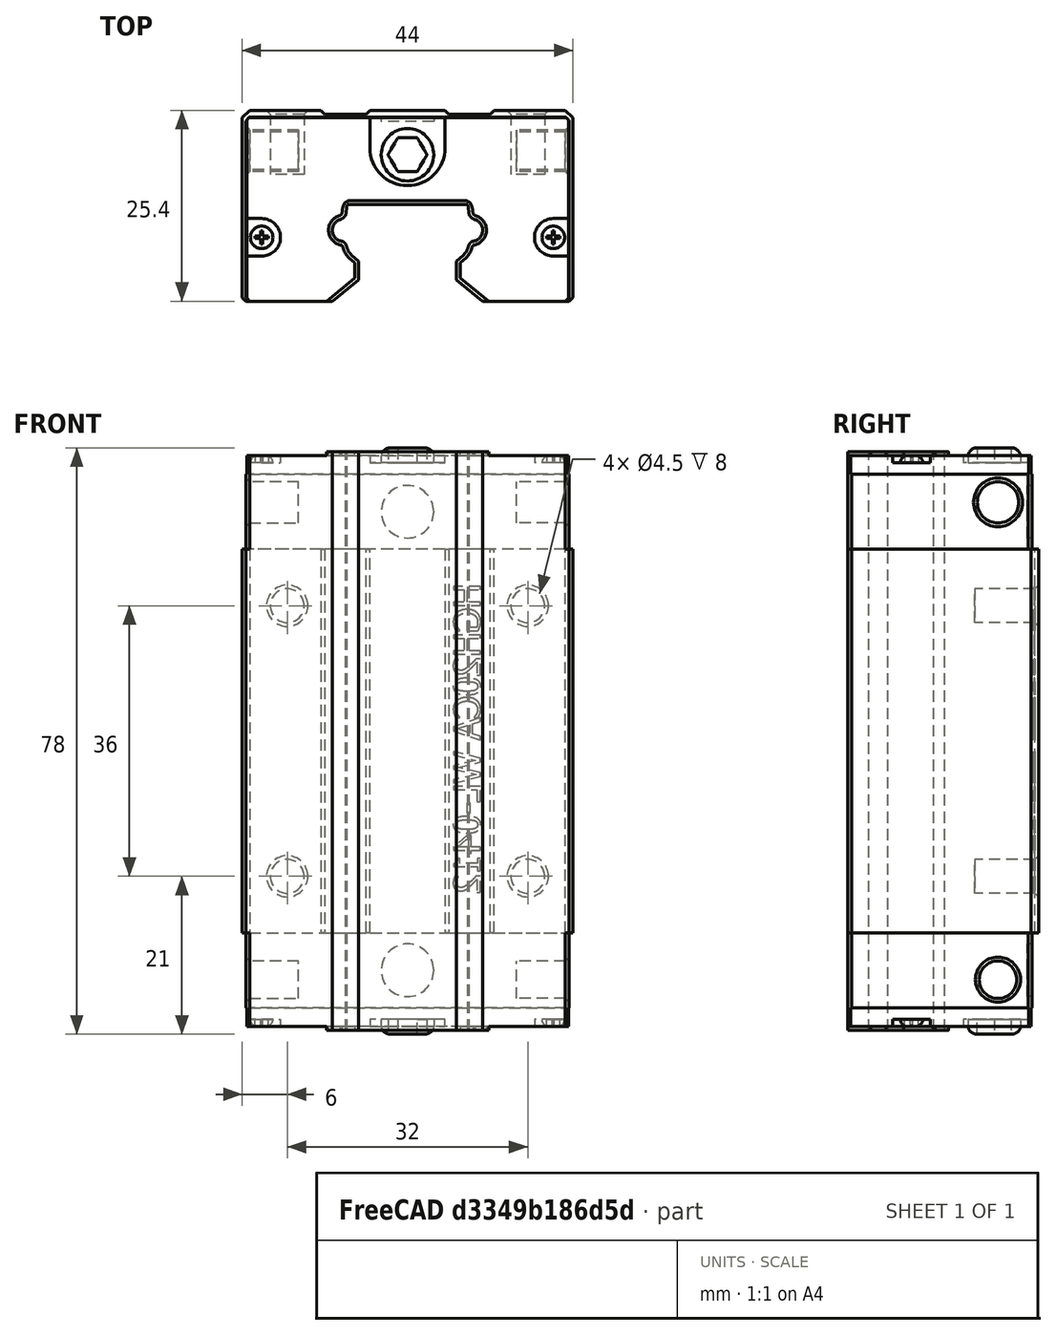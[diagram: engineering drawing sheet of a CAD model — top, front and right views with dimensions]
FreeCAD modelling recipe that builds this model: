
FCSTD DOCUMENT  (FreeCAD 0.22R37100 (Git))
Label: HGH20CA
License: All rights reserved
LicenseURL: http://en.wikipedia.org/wiki/All_rights_reserved
objects: PartDesign::CoordinateSystem×3, Part::Feature×1, PartDesign::FeatureBase×1, PartDesign::Body×1, Sketcher::SketchObject×1
note: 7 computed .brp shape members not serialized (recipe doc carries the construction recipe); baked Part::Feature solids carry a one-line shape summary decoded from their .brp

FEATURE [Part::Feature] Part__Feature004  label="HGH20CA"
  shape: bbox 44.01 x 25.41 x 78.01 mm, 462 faces (baked)
FEATURE [PartDesign::FeatureBase] BaseFeature
  BaseFeature = -> Part__Feature004
  Suppressed = false
FEATURE [PartDesign::CoordinateSystem] Local_CS
  AttacherType = Attacher::AttachEngine3D
  AttachmentSupport = -> [XY_Plane]
  MapMode = 5
FEATURE [PartDesign::CoordinateSystem] Local_CS001
  AttacherType = Attacher::AttachEngine3D
  AttachmentOffset = pos=(0,25.4,0) rot=(1,0,0;-1.5708rad)
  AttachmentSupport = -> [XY_Plane]
  MapMode = 5
  Placement = pos=(0,25.4,0) rot=(1,0,0;4.71239rad)
FEATURE [PartDesign::CoordinateSystem] Local_CS002
  AttacherType = Attacher::AttachEngine3D
  AttachmentSupport = -> [BaseFeature]
  MapMode = 5
  Placement = pos=(0,12.9,0) rot=(1,0,0;1.5708rad)
FEATURE [PartDesign::Body] Body
  BaseFeature = -> Part__Feature004
  Group = -> [BaseFeature,Local_CS,Local_CS001,Local_CS002]
  Origin = -> Origin
  Tip = -> BaseFeature
FEATURE [Sketcher::SketchObject] Sketch  label="fix"
  FullyConstrained = true
  sketch-geometry (4):
    g0: Circle CenterX=16 CenterY=18 CenterZ=0 NormalX=0 NormalY=0 NormalZ=1 AngleXU=0 Radius=2.25
    g1: Circle CenterX=16 CenterY=-18 CenterZ=0 NormalX=0 NormalY=0 NormalZ=1 AngleXU=0 Radius=2.25
    g2: Circle CenterX=-16 CenterY=-18 CenterZ=0 NormalX=0 NormalY=0 NormalZ=1 AngleXU=0 Radius=2.25
    g3: Circle CenterX=-16 CenterY=18 CenterZ=0 NormalX=0 NormalY=0 NormalZ=1 AngleXU=0 Radius=2.25
  constraints (9):
    c: Equal(g0,g1)
    c: Equal(g0,g2)
    c: Equal(g0,g3)
    c: Diameter(g0) = 4.5
    c: DistanceX(g0) = 16
    c: DistanceY(g0) = 18
    c: Symmetric(g0,g1,g-1)
    c: Symmetric(g0,g3,g-2)
    c: Symmetric(g0,g2,g-1)
